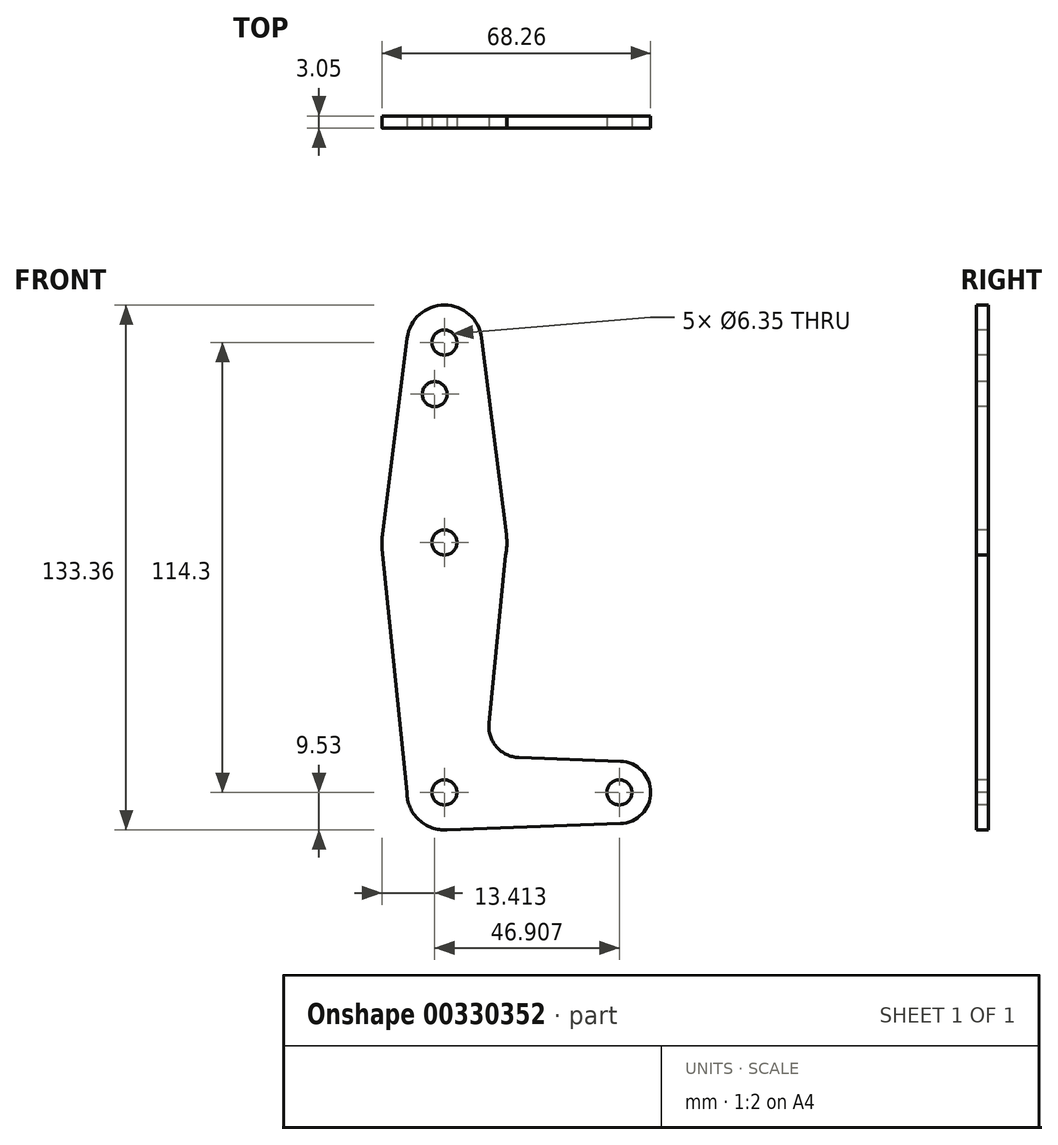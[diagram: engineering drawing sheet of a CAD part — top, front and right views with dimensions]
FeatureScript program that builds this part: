
annotation { "Feature Type Name" : "Feature", "Feature Type Description" : "" }
export const myFeature = defineFeature(function(context is Context, id is Id, definition is map)
    precondition{}
    {
        {
            var Q0;
            Q0=qCreatedBy(makeId("Front.planeOp"),FACE);
            var sketch = newSketch(context, id + "F0", { "sketchPlane" : qUnion([Q0])});
            skLineSegment(sketch, "E0", {"start": v(0, 0) * mm, "end": v(0, 114.3) * mm, "construction": true});
            skLineSegment(sketch, "E1", {"start": v(0, 0) * mm, "end": v(44.45, 0) * mm, "construction": true});
            skCircle(sketch, "E2", {"center": v(0, 114.3) * mm, "radius": 9.53 * mm});
            skCircle(sketch, "E3", {"center": v(0, 0) * mm, "radius": 9.53 * mm});
            skCircle(sketch, "E4", {"center": v(44.45, 0) * mm, "radius": 7.94 * mm});
            skLineSegment(sketch, "E5", {"start": v(0, -9.53) * mm, "end": v(44.73, -7.93) * mm});
            skPoint(sketch, "E5.startSnap0", {"position": v(0, 57.15) * mm});
            skCircle(sketch, "E6", {"center": v(0, 114.3) * mm, "radius": 3.18 * mm});
            skCircle(sketch, "E7", {"center": v(44.45, 0) * mm, "radius": 3.18 * mm});
            skCircle(sketch, "E8", {"center": v(0, 0) * mm, "radius": 3.18 * mm});
            skCircle(sketch, "E9", {"center": v(0, 63.5) * mm, "radius": 3.18 * mm});
            skLineSegment(sketch, "E10", {"start": v(18.94, 8.85) * mm, "end": v(44.73, 7.93) * mm});
            skCircle(sketch, "E11", {"center": v(-2.46, 101.17) * mm, "radius": 3.18 * mm});
            skArc(sketch, "E12.filletArc", {"start": v(11.32, 17.6) * mm, "mid": v(13.24, 11.57) * mm, "end": v(18.94, 8.85) * mm});
            skCircle(sketch, "E13", {"center": v(0, 63.5) * mm, "radius": 15.88 * mm});
            skLineSegment(sketch, "E14", {"start": v(15.88, 63.5) * mm, "end": v(9.57, 0) * mm});
            skPoint(sketch, "E15.orphan", {"position": v(-9.52, 0) * mm});
            skLineSegment(sketch, "E16", {"start": v(-15.8, 61.9) * mm, "end": v(-9.52, 0) * mm});
            skLineSegment(sketch, "E17", {"start": v(-15.75, 65.48) * mm, "end": v(-9.45, 115.5) * mm});
            skLineSegment(sketch, "E18", {"start": v(9.45, 115.5) * mm, "end": v(15.75, 65.48) * mm});
            skSolve(sketch);
        }
        {
            var Q0;
            Q0 = qSketchRegion(id + "F0", true);
            extrude(context, id + "F1", {"entities" : qUnion([Q0]), "oppositeDirection" : true, "depth" : 3.05 * mm});
        }
    });
